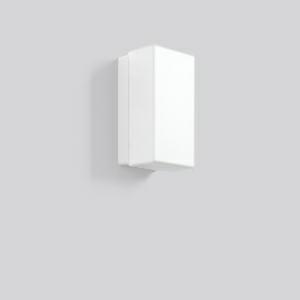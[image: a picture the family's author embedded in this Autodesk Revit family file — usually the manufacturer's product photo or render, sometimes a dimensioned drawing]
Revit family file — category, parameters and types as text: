
# Revit family: rechteck_20146_002_0a68
name_source: partatom
category: Lighting Fixtures
units: mm (PartAtom-declared; Revit-internal decimal feet)

## family parameters
Cut with Voids When Loaded = No
Host = Face
Light Source = No
Part Type = Normal
Room Calculation Point = No
Round Connector Dimension = Use Diameter
Shared = No

## types (1)
- RECHTECK (1 x QA60/clear E27, 700 lm, 46 W, 3000)
    Apparent Load = 46 VA
    CIE Flux Codes = 34 63 85 72 42
    Color Rendering = 90
    Color Temperature = 3000
    Default Elevation = 1800 mm
    Description = Series: RECHTECK
Rectangular surface-mounted luminaire in classic design. Base: plastic. Opal glass: mouth blown, silk finish. Diffuser fastening: spring system. Suitable for Ceiling mounting, Wall (surface). IP 43 ceiling mounting, IP 44 wall mounting. 
Colour: white
Length: 220 mm
Width: 120 mm
Height: 105 mm
Lamp: A60
Number of lamps: 1
Wattage: 60 W
Socket: E27
System power: 46 W
Rated luminous flux: 300 lm
Luminous efficiency: 7 lm/W
Control gear: Converter not necessary
Protection class: II
Type of protection: IP 43
    Height = 105 mm
    Lamp = 1 x QA60/clear E27
    Lamp Light Flux = 700 lm
    Lamp Power = 46 W
    Lamp count = 1
    Length = 220 mm
    Lifetime = 3000 h
    Luminous efficacy = 6 lm/W
    Manufacturer = RZB
    ModVariant = No
    Model = 20146.002
    Mounting Place = Ceiling, Wall
    Mounting Type = Surface mounted
    Number of Poles = 1
    OnlyDefault = Yes
    Power Factor = 1
    Product Name = RECHTECK
    Product group = Surface mounted ceiling and wall luminaires
    ProductGroupID = 305
    Protection Class = Protection class II
    Protection Degree = IP 43
    RLX_Detail_Level = 1
    RLX_Emergency_Light_Flux = 0 lm
    RLX_Emergency_Type = 0
    RLX_Emergency_Type_DB = No
    RlxData = <blob elided: 19649 chars, md5=3c6a8a47>
    Socket = E27
    Standby Power = 0 W
    System Light Flux = 297 lm
    System Power = 46 W
    Type Comments = Product without accessories
    Type Image = 21146.002.jpg
    URL = http://relux.com
    VarID = ---
    Voltage = 230 V
    Voltage Range = 220-240 V
    Weight = 0.00 kg
    Width = 120 mm

## geometry (parser evidence)
native form markers: Blend x4, Sweep x14
no freeform markers — native parametric forms only
